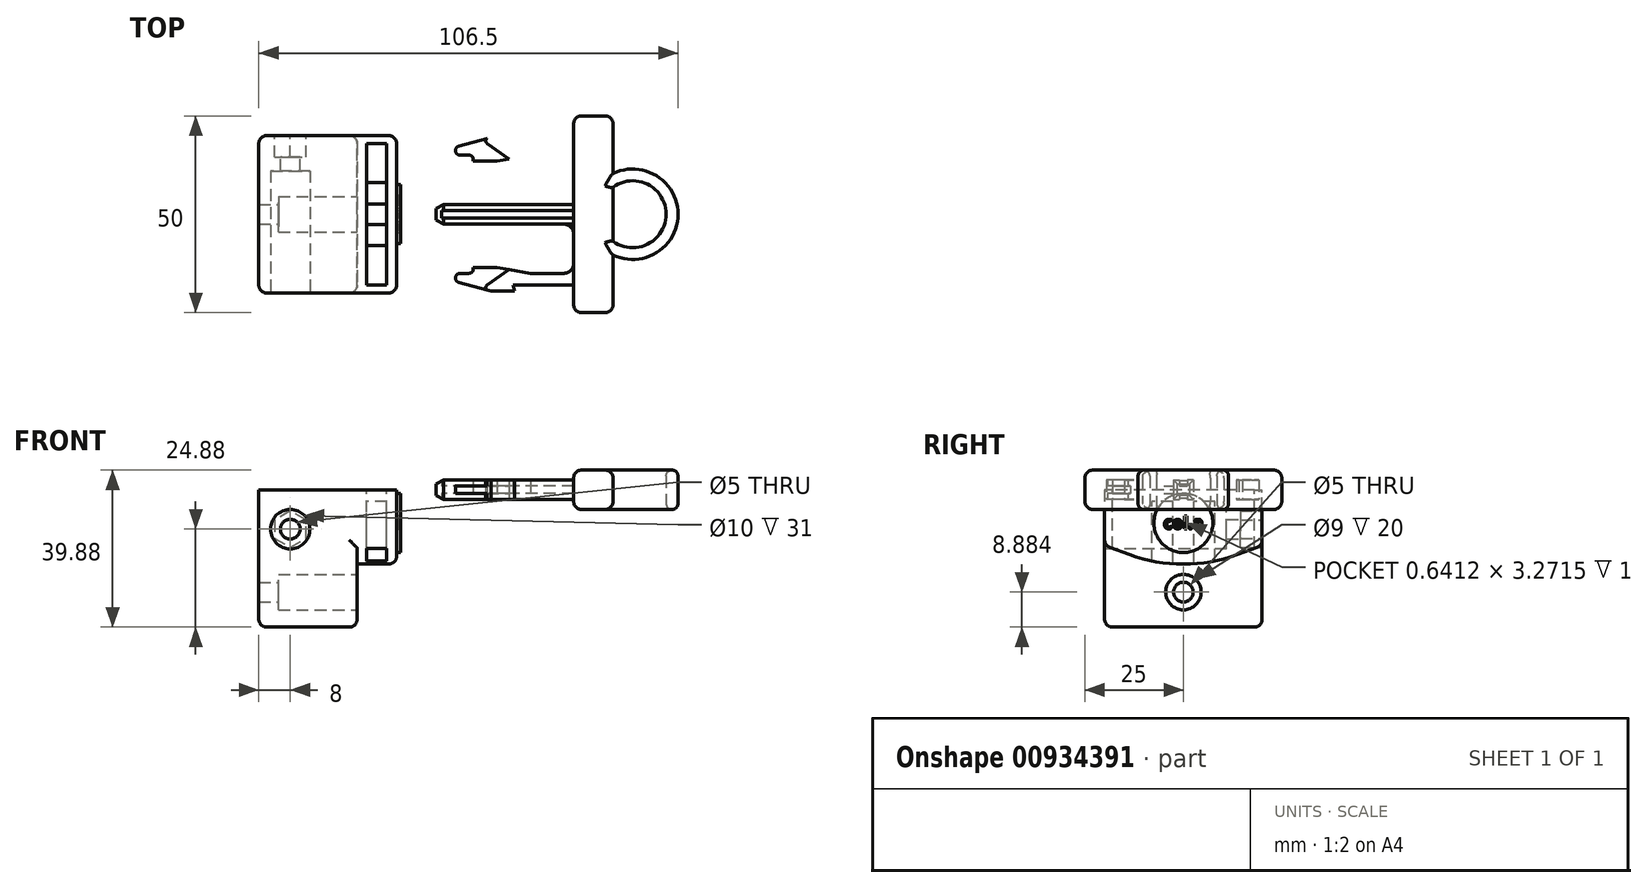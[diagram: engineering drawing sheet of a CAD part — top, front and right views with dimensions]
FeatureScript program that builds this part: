
annotation { "Feature Type Name" : "Feature", "Feature Type Description" : "" }
export const myFeature = defineFeature(function(context is Context, id is Id, definition is map)
    precondition{}
    {
        {
            var Q0;
            Q0=qCreatedBy(makeId("Top.planeOp"),FACE);
            var sketch = newSketch(context, id + "F0", { "sketchPlane" : qUnion([Q0])});
            skLineSegment(sketch, "E0.bottom", {"start": v(5, -25) * mm, "end": v(-5, -25) * mm});
            skLineSegment(sketch, "E0.top", {"start": v(5, 25) * mm, "end": v(-5, 25) * mm});
            skLineSegment(sketch, "E0.left", {"start": v(5, -25) * mm, "end": v(5, 25) * mm});
            skLineSegment(sketch, "E0.right", {"start": v(-5, -12.5) * mm, "end": v(-5, 12.5) * mm});
            skPoint(sketch, "E0.middle", {"position": v(0, 0) * mm});
            skLineSegment(sketch, "E1", {"start": v(-5, -18) * mm, "end": v(-20.4, -18) * mm});
            skLineSegment(sketch, "E2", {"start": v(-20.4, -18) * mm, "end": v(-20, -19.5) * mm});
            skLineSegment(sketch, "E3", {"start": v(-20, -19.5) * mm, "end": v(-26, -19.5) * mm});
            skLineSegment(sketch, "E4", {"start": v(-5, 0) * mm, "end": v(5, 0) * mm, "construction": true});
            skLineSegment(sketch, "E5.bottom", {"start": v(-5, 2.5) * mm, "end": v(-40, 2.5) * mm});
            skLineSegment(sketch, "E5.top", {"start": v(-5, -2.5) * mm, "end": v(-40, -2.5) * mm});
            skLineSegment(sketch, "E5.left", {"start": v(-5, 2.5) * mm, "end": v(-5, -2.5) * mm});
            skLineSegment(sketch, "E5.right", {"start": v(-40, 2.5) * mm, "end": v(-40, -2.5) * mm});
            skLineSegment(sketch, "E6", {"start": v(-7.5, -15) * mm, "end": v(-16, -15) * mm});
            skLineSegment(sketch, "E7", {"start": v(-16, -15) * mm, "end": v(-24.5, -13.5) * mm});
            skLineSegment(sketch, "E8", {"start": v(-24.5, -13.5) * mm, "end": v(-30.5, -13.5) * mm});
            skLineSegment(sketch, "E9", {"start": v(-30.5, -13.5) * mm, "end": v(-30.5, -14) * mm});
            skLineSegment(sketch, "E10", {"start": v(-31.5, -15) * mm, "end": v(-33.83, -15) * mm});
            skLineSegment(sketch, "E11", {"start": v(-34.14, -17.32) * mm, "end": v(-26, -19.5) * mm});
            skPoint(sketch, "E12.newPointA", {"position": v(-36.5, -15) * mm});
            skArc(sketch, "E12.filletArc", {"start": v(-33.83, -15) * mm, "mid": v(-35, -16.03) * mm, "end": v(-34.14, -17.32) * mm});
            skPoint(sketch, "E13.visualSharp", {"position": v(-30.5, -15) * mm});
            skArc(sketch, "E13.filletArc", {"start": v(-31.5, -15) * mm, "mid": v(-30.8, -14.7) * mm, "end": v(-30.5, -14) * mm});
            skLineSegment(sketch, "E14", {"start": v(-21.37, -14.05) * mm, "end": v(-27.01, -18) * mm});
            skArc(sketch, "E15", {"start": v(-27.01, -18) * mm, "mid": v(-27.33, -18.61) * mm, "end": v(-27.01, -19.23) * mm});
            skArc(sketch, "E16.MirrorCS", {"start": v(-31.5, 15) * mm, "mid": v(-30.8, 14.7) * mm, "end": v(-30.5, 14) * mm});
            skLineSegment(sketch, "E17.MirrorCS", {"start": v(-30.5, 13.5) * mm, "end": v(-30.5, 14) * mm});
            skArc(sketch, "E18.MirrorCS", {"start": v(-27.01, 18) * mm, "mid": v(-27.33, 18.61) * mm, "end": v(-27.01, 19.23) * mm});
            skLineSegment(sketch, "E19.MirrorCS", {"start": v(-20.4, 18) * mm, "end": v(-20, 19.5) * mm});
            skLineSegment(sketch, "E20.MirrorCS", {"start": v(-31.5, 15) * mm, "end": v(-33.83, 15) * mm});
            skLineSegment(sketch, "E21.MirrorCS", {"start": v(-20, 19.5) * mm, "end": v(-26, 19.5) * mm});
            skArc(sketch, "E22.MirrorCS", {"start": v(-33.83, 15) * mm, "mid": v(-35, 16.03) * mm, "end": v(-34.14, 17.32) * mm});
            skLineSegment(sketch, "E23.MirrorCS", {"start": v(-24.5, 13.5) * mm, "end": v(-30.5, 13.5) * mm});
            skPoint(sketch, "E24.MirrorP", {"position": v(-36.5, 15) * mm});
            skLineSegment(sketch, "E25.MirrorCS", {"start": v(-16, 15) * mm, "end": v(-24.5, 13.5) * mm});
            skLineSegment(sketch, "E26.MirrorCS", {"start": v(-5, 18) * mm, "end": v(-20.4, 18) * mm});
            skPoint(sketch, "E27.MirrorP", {"position": v(-30.5, 15) * mm});
            skLineSegment(sketch, "E28.MirrorCS", {"start": v(-7.5, 15) * mm, "end": v(-16, 15) * mm});
            skLineSegment(sketch, "E29.MirrorCS", {"start": v(-34.14, 17.32) * mm, "end": v(-26, 19.5) * mm});
            skLineSegment(sketch, "E30.MirrorCS", {"start": v(-21.37, 14.05) * mm, "end": v(-27.01, 18) * mm});
            skArc(sketch, "E31", {"start": v(-5, -5) * mm, "mid": v(-5.73, -3.23) * mm, "end": v(-7.5, -2.5) * mm});
            skArc(sketch, "E32.MirrorCS", {"start": v(-5, 5) * mm, "mid": v(-5.73, 3.23) * mm, "end": v(-7.5, 2.5) * mm});
            skPoint(sketch, "E33.newPointB", {"position": v(-5, -20) * mm});
            skArc(sketch, "E33.filletArc", {"start": v(-7.5, -15) * mm, "mid": v(-5.73, -14.27) * mm, "end": v(-5, -12.5) * mm});
            skPoint(sketch, "E34.newPointB", {"position": v(-5, 20) * mm});
            skArc(sketch, "E34.filletArc", {"start": v(-5, 12.5) * mm, "mid": v(-5.73, 14.27) * mm, "end": v(-7.5, 15) * mm});
            skLineSegment(sketch, "E35", {"start": v(-5, 18) * mm, "end": v(-5, 12.5) * mm});
            skLineSegment(sketch, "E36", {"start": v(-5, -12.5) * mm, "end": v(-5, -18) * mm});
            skLineSegment(sketch, "E37", {"start": v(-5, 25) * mm, "end": v(-5, 18) * mm});
            skLineSegment(sketch, "E38", {"start": v(-5, -25) * mm, "end": v(-5, -18) * mm});
            skLineSegment(sketch, "E39", {"start": v(-35.01, -19.06) * mm, "end": v(-35.01, -34.69) * mm, "construction": true});
            skLineSegment(sketch, "E40.0", {"start": v(-5, -1) * mm, "end": v(-38.5, -1) * mm});
            skLineSegment(sketch, "E40.2", {"start": v(-5, 1) * mm, "end": v(-38.5, 1) * mm});
            skLineSegment(sketch, "E40.3", {"start": v(-38.5, 1) * mm, "end": v(-38.5, -1) * mm});
            skSolve(sketch);
        }
        {
            var Q0;
            Q0=makeQuery(id+"F0.imprint","IMPRINT",FACE,{"disambiguationData":[TD([[makeQuery(id+"F0.imprint","IMPRINT",EDGE,{"derivedFrom":sQuery(id+"F0.wireOp",EDGE,"E0.bottom")}),-1.0]])]});
            extrude(context, id + "F1", {"entities" : qUnion([Q0]), "endBound" : BoundingType.SYMMETRIC, "depth" : 10 * mm, "offsetDistance" : 25 * mm});
        }
        {
            var Q0;
            Q0=makeQuery(id+"F0.imprint","IMPRINT",FACE,{"disambiguationData":[TD([[makeQuery(id+"F0.imprint","IMPRINT",EDGE,{"derivedFrom":sQuery(id+"F0.wireOp",EDGE,"E16.MirrorCS")}),1.0]])]});
            var Q1;
            {var subQ5=sQuery(id+"F0.wireOp",EDGE,"E18.MirrorCS");Q1=makeQuery(id+"F0.imprint","IMPRINT",FACE,{"disambiguationData":[TD([[makeQuery(id+"F0.imprint","IMPRINT",EDGE,{"derivedFrom":subQ5}),-1.0]])]});}
            var Q2;
            {var subQ0=sQuery(id+"F0.wireOp",EDGE,"E8");Q2=makeQuery(id+"F0.imprint","IMPRINT",FACE,{"disambiguationData":[TD([[makeQuery(id+"F0.imprint","IMPRINT",EDGE,{"derivedFrom":subQ0}),1.0]])]});}
            var Q3;
            Q3=makeQuery(id+"F0.imprint","IMPRINT",FACE,{"disambiguationData":[TD([[makeQuery(id+"F0.imprint","IMPRINT",EDGE,{"derivedFrom":sQuery(id+"F0.wireOp",EDGE,"E1")}),-1.0]])]});
            var Q4;
            {var subQ3=sQuery(id+"F0.wireOp",EDGE,"E32.MirrorCS");Q4=makeQuery(id+"F0.imprint","IMPRINT",FACE,{"disambiguationData":[TD([[makeQuery(id+"F0.imprint","IMPRINT",EDGE,{"derivedFrom":subQ3}),1.0]])]});}
            var Q5;
            {var subQ3=sQuery(id+"F0.wireOp",EDGE,"E31");Q5=makeQuery(id+"F0.imprint","IMPRINT",FACE,{"disambiguationData":[TD([[makeQuery(id+"F0.imprint","IMPRINT",EDGE,{"derivedFrom":subQ3}),-1.0]])]});}
            var Q6;
            Q6=makeQuery(id+"F0.imprint","IMPRINT",FACE,{"disambiguationData":[TD([[makeQuery(id+"F0.imprint","IMPRINT",EDGE,{"derivedFrom":sQuery(id+"F0.wireOp",EDGE,"E40.0")}),-1.0]])]});
            extrude(context, id + "F2", {"entities" : qUnion([Q0, Q1, Q2, Q3, Q4, Q5, Q6]), "operationType" : NewBodyOperationType.ADD, "endBound" : BoundingType.SYMMETRIC, "depth" : 2 * mm, "offsetDistance" : 25 * mm});
        }
        {
            var Q0;
            {var subQ5=sQuery(id+"F0.wireOp",EDGE,"E18.MirrorCS");Q0=makeQuery(id+"F0.imprint","IMPRINT",FACE,{"disambiguationData":[TD([[makeQuery(id+"F0.imprint","IMPRINT",EDGE,{"derivedFrom":subQ5}),-1.0]])]});}
            var Q1;
            Q1=makeQuery(id+"F0.imprint","IMPRINT",FACE,{"disambiguationData":[TD([[makeQuery(id+"F0.imprint","IMPRINT",EDGE,{"derivedFrom":sQuery(id+"F0.wireOp",EDGE,"E1")}),-1.0]])]});
            var Q2;
            Q2=makeQuery(id+"F0.imprint","IMPRINT",FACE,{"disambiguationData":[TD([[makeQuery(id+"F0.imprint","IMPRINT",EDGE,{"derivedFrom":sQuery(id+"F0.wireOp",EDGE,"E5.bottom")}),1.0]])]});
            extrude(context, id + "F3", {"entities" : qUnion([Q0, Q1, Q2]), "operationType" : NewBodyOperationType.ADD, "endBound" : BoundingType.SYMMETRIC, "depth" : 5 * mm, "offsetDistance" : 25 * mm});
        }
        {
            var Q0;
            Q0=makeQuery(id+"F3.opExtrude","CAP_EDGE",EDGE,{"disambiguationData":[OSD([sQuery(id+"F0.wireOp",EDGE,"E5.right")])],"isStart":true});
            var Q1;
            Q1=makeQuery(id+"F3.opExtrude","SWEPT_EDGE",EDGE,{"disambiguationData":[OSD([sQuery(id+"F0.wireOp",EDGE,"E5.top"),sQuery(id+"F0.wireOp",EDGE,"E5.right")])]});
            var Q2;
            Q2=makeQuery(id+"F3.opExtrude","CAP_EDGE",EDGE,{"disambiguationData":[OSD([sQuery(id+"F0.wireOp",EDGE,"E5.right")])],"isStart":false});
            var Q3;
            Q3=makeQuery(id+"F3.opExtrude","SWEPT_EDGE",EDGE,{"disambiguationData":[OSD([sQuery(id+"F0.wireOp",EDGE,"E5.bottom"),sQuery(id+"F0.wireOp",EDGE,"E5.right")])]});
            chamfer(context, id + "F4", {"entities" : qUnion([Q0, Q1, Q2, Q3]), "chamferType" : ChamferType.TWO_OFFSETS, "width1" : 1 * mm, "oppositeDirection" : false, "width2" : 2 * mm, "tangentPropagation" : true});
        }
        {
            var Q0;
            Q0=makeQuery(id+"F1.opExtrude","CAP_EDGE",EDGE,{"disambiguationData":[OSD([sQuery(id+"F0.wireOp",EDGE,"E0.bottom")])],"isStart":true});
            var Q1;
            Q1=makeQuery(id+"F1.opExtrude","CAP_EDGE",EDGE,{"disambiguationData":[OSD([sQuery(id+"F0.wireOp",EDGE,"E0.right"),sQuery(id+"F0.wireOp",EDGE,"E5.left"),sQuery(id+"F0.wireOp",EDGE,"E35"),sQuery(id+"F0.wireOp",EDGE,"E36"),sQuery(id+"F0.wireOp",EDGE,"E37"),sQuery(id+"F0.wireOp",EDGE,"E38")])],"isStart":true});
            var Q2;
            Q2=makeQuery(id+"F1.opExtrude","CAP_EDGE",EDGE,{"disambiguationData":[OSD([sQuery(id+"F0.wireOp",EDGE,"E0.left")])],"isStart":true});
            var Q3;
            Q3=makeQuery(id+"F1.opExtrude","SWEPT_EDGE",EDGE,{"disambiguationData":[OSD([sQuery(id+"F0.wireOp",EDGE,"E0.bottom"),sQuery(id+"F0.wireOp",EDGE,"E38")])]});
            var Q4;
            Q4=makeQuery(id+"F1.opExtrude","SWEPT_EDGE",EDGE,{"disambiguationData":[OSD([sQuery(id+"F0.wireOp",EDGE,"E0.bottom"),sQuery(id+"F0.wireOp",EDGE,"E0.left")])]});
            var Q5;
            Q5=makeQuery(id+"F1.opExtrude","CAP_EDGE",EDGE,{"disambiguationData":[OSD([sQuery(id+"F0.wireOp",EDGE,"E0.bottom")])],"isStart":false});
            var Q6;
            Q6=makeQuery(id+"F1.opExtrude","CAP_EDGE",EDGE,{"disambiguationData":[OSD([sQuery(id+"F0.wireOp",EDGE,"E0.left")])],"isStart":false});
            var Q7;
            Q7=makeQuery(id+"F1.opExtrude","CAP_EDGE",EDGE,{"disambiguationData":[OSD([sQuery(id+"F0.wireOp",EDGE,"E0.top")])],"isStart":false});
            var Q8;
            Q8=makeQuery(id+"F1.opExtrude","CAP_EDGE",EDGE,{"disambiguationData":[OSD([sQuery(id+"F0.wireOp",EDGE,"E0.right"),sQuery(id+"F0.wireOp",EDGE,"E5.left"),sQuery(id+"F0.wireOp",EDGE,"E35"),sQuery(id+"F0.wireOp",EDGE,"E36"),sQuery(id+"F0.wireOp",EDGE,"E37"),sQuery(id+"F0.wireOp",EDGE,"E38")])],"isStart":false});
            var Q9;
            Q9=makeQuery(id+"F1.opExtrude","SWEPT_EDGE",EDGE,{"disambiguationData":[OSD([sQuery(id+"F0.wireOp",EDGE,"E0.top"),sQuery(id+"F0.wireOp",EDGE,"E37")])]});
            var Q10;
            Q10=makeQuery(id+"F1.opExtrude","SWEPT_EDGE",EDGE,{"disambiguationData":[OSD([sQuery(id+"F0.wireOp",EDGE,"E0.top"),sQuery(id+"F0.wireOp",EDGE,"E0.left")])]});
            var Q11;
            Q11=makeQuery(id+"F1.opExtrude","CAP_EDGE",EDGE,{"disambiguationData":[OSD([sQuery(id+"F0.wireOp",EDGE,"E0.top")])],"isStart":true});
            fillet(context, id + "F5", {"entities" : qUnion([Q0, Q1, Q2, Q3, Q4, Q5, Q6, Q7, Q8, Q9, Q10, Q11]), "radius" : 2 * mm, "tangentPropagation" : true, "allowEdgeOverflow" : false});
        }
        {
            var Q0;
            Q0=qCreatedBy(makeId("Front.planeOp"),FACE);
            var sketch = newSketch(context, id + "F6", { "sketchPlane" : qUnion([Q0])});
            skLineSegment(sketch, "E41.bottom", {"start": v(0, -5) * mm, "end": v(0, -5) * mm});
            skLineSegment(sketch, "E41.top", {"start": v(0, 5) * mm, "end": v(0, 5) * mm});
            skLineSegment(sketch, "E41.left", {"start": v(1.5, -3.5) * mm, "end": v(1.5, 3.5) * mm});
            skLineSegment(sketch, "E41.right", {"start": v(-1.5, -3.5) * mm, "end": v(-1.5, 3.5) * mm});
            skPoint(sketch, "E41.middle", {"position": v(0, 0) * mm});
            skPoint(sketch, "E42.visualSharp", {"position": v(-1.5, 5) * mm});
            skArc(sketch, "E42.filletArc", {"start": v(0, 5) * mm, "mid": v(-1.06, 4.56) * mm, "end": v(-1.5, 3.5) * mm});
            skPoint(sketch, "E43.visualSharp", {"position": v(1.5, 5) * mm});
            skArc(sketch, "E43.filletArc", {"start": v(1.5, 3.5) * mm, "mid": v(1.06, 4.56) * mm, "end": v(0, 5) * mm});
            skPoint(sketch, "E44.visualSharp", {"position": v(1.5, -5) * mm});
            skArc(sketch, "E44.filletArc", {"start": v(0, -5) * mm, "mid": v(1.06, -4.56) * mm, "end": v(1.5, -3.5) * mm});
            skPoint(sketch, "E45.visualSharp", {"position": v(-1.5, -5) * mm});
            skArc(sketch, "E45.filletArc", {"start": v(-1.5, -3.5) * mm, "mid": v(-1.06, -4.56) * mm, "end": v(0, -5) * mm});
            skLineSegment(sketch, "E46", {"start": v(0, 0) * mm, "end": v(10, 0) * mm, "construction": true});
            skLineSegment(sketch, "E47", {"start": v(10, 0) * mm, "end": v(10, 4.4) * mm, "construction": true});
            skSolve(sketch);
        }
        {
            var Q0;
            Q0 = qSketchRegion(id + "F6", true);
            var Q1;
            Q1=sQuery(id+"F6.wireOp",EDGE,"E47");
            revolve(context, id + "F7", {"operationType" : NewBodyOperationType.ADD, "surfaceOperationType" : NewSurfaceOperationType.NEW, "entities" : qUnion([Q0]), "axis" : qUnion([Q1]), "revolveType" : RevolveType.FULL});
        }
        {
            var Q0;
            Q0=qCreatedBy(makeId("Top.planeOp"),FACE);
            var sketch = newSketch(context, id + "F8", { "sketchPlane" : qUnion([Q0])});
            skLineSegment(sketch, "E48.bottom", {"start": v(-52.5, -2.65) * mm, "end": v(-57.6, -2.65) * mm});
            skLineSegment(sketch, "E48.top", {"start": v(-52.5, 2.65) * mm, "end": v(-57.6, 2.65) * mm});
            skLineSegment(sketch, "E48.left", {"start": v(-52.5, -2.65) * mm, "end": v(-52.5, 2.65) * mm});
            skLineSegment(sketch, "E48.right", {"start": v(-57.6, -2.65) * mm, "end": v(-57.6, 2.65) * mm});
            skPoint(sketch, "E48.middle", {"position": v(-55.05, 0) * mm});
            skLineSegment(sketch, "E49.bottom", {"start": v(-52.5, 18) * mm, "end": v(-57.6, 18) * mm});
            skLineSegment(sketch, "E49.top", {"start": v(-52.5, 8) * mm, "end": v(-57.6, 8) * mm});
            skLineSegment(sketch, "E49.left", {"start": v(-52.5, 18) * mm, "end": v(-52.5, 8) * mm});
            skLineSegment(sketch, "E49.right", {"start": v(-57.6, 18) * mm, "end": v(-57.6, 8) * mm});
            skPoint(sketch, "E49.middle", {"position": v(-55.05, 13) * mm});
            skPoint(sketch, "E49.middle.positionSnap0", {"position": v(-55.05, 2.65) * mm});
            skPoint(sketch, "E49.centerSnap0", {"position": v(-55.05, 2.65) * mm});
            skLineSegment(sketch, "E50.bottom", {"start": v(-52.5, -18) * mm, "end": v(-57.6, -18) * mm});
            skLineSegment(sketch, "E50.top", {"start": v(-52.5, -8) * mm, "end": v(-57.6, -8) * mm});
            skLineSegment(sketch, "E50.left", {"start": v(-52.5, -18) * mm, "end": v(-52.5, -8) * mm});
            skLineSegment(sketch, "E50.right", {"start": v(-57.6, -18) * mm, "end": v(-57.6, -8) * mm});
            skPoint(sketch, "E50.middle", {"position": v(-55.05, -13) * mm});
            skLineSegment(sketch, "E51.bottom", {"start": v(-57.6, 18) * mm, "end": v(-52.5, 18) * mm});
            skLineSegment(sketch, "E51.top", {"start": v(-57.6, -18) * mm, "end": v(-52.5, -18) * mm});
            skLineSegment(sketch, "E51.left", {"start": v(-57.6, 18) * mm, "end": v(-57.6, -18) * mm});
            skLineSegment(sketch, "E51.right", {"start": v(-52.5, 18) * mm, "end": v(-52.5, -18) * mm});
            skLineSegment(sketch, "E52", {"start": v(-50, 28.03) * mm, "end": v(-50, -31.97) * mm, "construction": true});
            skLineSegment(sketch, "E53", {"start": v(0, 0) * mm, "end": v(-100, 0) * mm, "construction": true});
            skSolve(sketch);
        }
        {
            var Q0;
            Q0=sQuery(id+"F8.wireOp",EDGE,"E52");
            cPlane(context, id + "F9", {"entities" : qUnion([Q0]), "cplaneType" : CPlaneType.LINE_ANGLE, "offset" : 25 * mm, "angle" : 90 * degree, "width" : 150 * mm, "height" : 150 * mm});
        }
        {
            var Q0;
            Q0=qCreatedBy(id+"F9.planeOp",FACE);
            var sketch = newSketch(context, id + "F10", { "sketchPlane" : qUnion([Q0])});
            skLineSegment(sketch, "E54", {"start": v(20, 0) * mm, "end": v(-20, 0) * mm});
            skLineSegment(sketch, "E55", {"start": v(-20, 0) * mm, "end": v(-20, -14.17) * mm});
            skLineSegment(sketch, "E56", {"start": v(-20, -14.17) * mm, "end": v(-13.68, -16.47) * mm});
            skLineSegment(sketch, "E57", {"start": v(13.68, -16.47) * mm, "end": v(20, -14.17) * mm});
            skLineSegment(sketch, "E58", {"start": v(20, -14.17) * mm, "end": v(20, 0) * mm});
            skPoint(sketch, "E59.visualSharp", {"position": v(0, -21.45) * mm});
            skArc(sketch, "E59.filletArc", {"start": v(-13.68, -16.47) * mm, "mid": v(0, -18.88) * mm, "end": v(13.68, -16.47) * mm});
            skLineSegment(sketch, "E60", {"start": v(-18, 0) * mm, "end": v(-18, -14.9) * mm, "construction": true});
            skSolve(sketch);
        }
        {
            var Q0;
            Q0 = qSketchRegion(id + "F10", true);
            extrude(context, id + "F11", {"entities" : qUnion([Q0]), "oppositeDirection" : true, "depth" : 10 * mm, "offsetDistance" : 25 * mm});
        }
        {
            var Q0;
            {var subQ0=sQuery(id+"F8.wireOp",EDGE,"E49.top");Q0=makeQuery(id+"F8.imprint","IMPRINT",FACE,{"disambiguationData":[TD([[makeQuery(id+"F8.imprint","IMPRINT",EDGE,{"derivedFrom":subQ0}),-1.0]])]});}
            var Q1;
            {var subQ0=sQuery(id+"F8.wireOp",EDGE,"E48.bottom");Q1=makeQuery(id+"F8.imprint","IMPRINT",FACE,{"disambiguationData":[TD([[makeQuery(id+"F8.imprint","IMPRINT",EDGE,{"derivedFrom":subQ0}),-1.0]])]});}
            var Q2;
            {var subQ0=sQuery(id+"F8.wireOp",EDGE,"E50.top");Q2=makeQuery(id+"F8.imprint","IMPRINT",FACE,{"disambiguationData":[TD([[makeQuery(id+"F8.imprint","IMPRINT",EDGE,{"derivedFrom":subQ0}),1.0]])]});}
            extrude(context, id + "F12", {"entities" : qUnion([Q0, Q1, Q2]), "operationType" : NewBodyOperationType.REMOVE, "endBound" : BoundingType.THROUGH_ALL, "oppositeDirection" : true, "depth" : 25 * mm, "offsetDistance" : 25 * mm});
        }
        {
            var Q0;
            Q0=makeQuery(id+"F11.opExtrude","CAP_FACE",FACE,{"disambiguationData":[OSD([sQuery(id+"F10.wireOp",EDGE,"E54"),sQuery(id+"F10.wireOp",EDGE,"E55"),sQuery(id+"F10.wireOp",EDGE,"E56"),sQuery(id+"F10.wireOp",EDGE,"E57"),sQuery(id+"F10.wireOp",EDGE,"E58"),sQuery(id+"F10.wireOp",EDGE,"E59.filletArc")])],"isStart":false});
            var sketch = newSketch(context, id + "F13", { "sketchPlane" : qUnion([Q0])});
            skLineSegment(sketch, "E61.bottom", {"start": v(-20, 0) * mm, "end": v(20, 0) * mm});
            skLineSegment(sketch, "E61.top", {"start": v(-20, -34.88) * mm, "end": v(20, -34.88) * mm});
            skLineSegment(sketch, "E61.left", {"start": v(-20, 0) * mm, "end": v(-20, -34.88) * mm});
            skLineSegment(sketch, "E61.right", {"start": v(20, 0) * mm, "end": v(20, -34.88) * mm});
            skSolve(sketch);
        }
        {
            var Q0;
            Q0 = qSketchRegion(id + "F13", true);
            extrude(context, id + "F14", {"entities" : qUnion([Q0]), "operationType" : NewBodyOperationType.ADD, "depth" : 25 * mm, "offsetDistance" : 25 * mm});
        }
        {
            var Q0;
            {var subQ0=sQuery(id+"F8.wireOp",EDGE,"E48.top");Q0=makeQuery(id+"F8.imprint","IMPRINT",FACE,{"disambiguationData":[TD([[makeQuery(id+"F8.imprint","IMPRINT",EDGE,{"derivedFrom":subQ0}),-1.0]])]});}
            var Q1;
            {var subQ0=sQuery(id+"F8.wireOp",EDGE,"E48.bottom");Q1=makeQuery(id+"F8.imprint","IMPRINT",FACE,{"disambiguationData":[TD([[makeQuery(id+"F8.imprint","IMPRINT",EDGE,{"derivedFrom":subQ0}),1.0]])]});}
            extrude(context, id + "F15", {"entities" : qUnion([Q0, Q1]), "operationType" : NewBodyOperationType.REMOVE, "oppositeDirection" : true, "depth" : 3 * mm, "offsetDistance" : 25 * mm});
        }
        {
            var Q0;
            Q0=makeQuery(id+"F11.opExtrude","SWEPT_EDGE",EDGE,{"disambiguationData":[OSD([sQuery(id+"F10.wireOp",EDGE,"E57"),sQuery(id+"F10.wireOp",EDGE,"E58")])]});
            var Q1;
            Q1=makeQuery(id+"F11.opExtrude","SWEPT_EDGE",EDGE,{"disambiguationData":[OSD([sQuery(id+"F10.wireOp",EDGE,"E55"),sQuery(id+"F10.wireOp",EDGE,"E56")])]});
            var Q2;
            Q2=makeQuery(id+"F11.opExtrude","CAP_EDGE",EDGE,{"disambiguationData":[OSD([sQuery(id+"F10.wireOp",EDGE,"E59.filletArc")])],"isStart":true});
            var Q3;
            Q3=makeQuery(id+"F14.opExtrude","CAP_EDGE",EDGE,{"disambiguationData":[OSD([sQuery(id+"F13.wireOp",EDGE,"E61.left")])],"isStart":true});
            var Q4;
            Q4=makeQuery(id+"F14.opExtrude","CAP_EDGE",EDGE,{"disambiguationData":[OSD([sQuery(id+"F13.wireOp",EDGE,"E61.right")])],"isStart":true});
            var Q5;
            Q5=makeQuery(id+"F14.opExtrude","CAP_EDGE",EDGE,{"disambiguationData":[OSD([sQuery(id+"F13.wireOp",EDGE,"E61.top")])],"isStart":true});
            var Q6;
            Q6=makeQuery(id+"F14.opExtrude","SWEPT_EDGE",EDGE,{"disambiguationData":[OSD([sQuery(id+"F13.wireOp",EDGE,"E61.top"),sQuery(id+"F13.wireOp",EDGE,"E61.left")])]});
            var Q7;
            Q7=makeQuery(id+"F14.opExtrude","SWEPT_EDGE",EDGE,{"disambiguationData":[OSD([sQuery(id+"F13.wireOp",EDGE,"E61.top"),sQuery(id+"F13.wireOp",EDGE,"E61.right")])]});
            var Q8;
            Q8=makeQuery(id+"F14.opExtrude","CAP_EDGE",EDGE,{"disambiguationData":[OSD([sQuery(id+"F13.wireOp",EDGE,"E61.top")])],"isStart":false});
            var Q9;
            Q9=makeQuery(id+"F14.opExtrude","CAP_EDGE",EDGE,{"disambiguationData":[OSD([sQuery(id+"F13.wireOp",EDGE,"E61.left")])],"isStart":false});
            var Q10;
            Q10=makeQuery(id+"F11.opExtrude","CAP_EDGE",EDGE,{"disambiguationData":[OSD([sQuery(id+"F10.wireOp",EDGE,"E58")])],"isStart":true});
            var Q11;
            Q11=makeQuery(id+"F11.opExtrude","CAP_EDGE",EDGE,{"disambiguationData":[OSD([sQuery(id+"F10.wireOp",EDGE,"E55")])],"isStart":true});
            var Q12;
            Q12=makeQuery(id+"F14.opExtrude","CAP_EDGE",EDGE,{"disambiguationData":[OSD([sQuery(id+"F13.wireOp",EDGE,"E61.right")])],"isStart":false});
            fillet(context, id + "F16", {"entities" : qUnion([Q0, Q1, Q2, Q3, Q4, Q5, Q6, Q7, Q8, Q9, Q10, Q11, Q12]), "radius" : 2 * mm, "tangentPropagation" : true, "allowEdgeOverflow" : false});
        }
        {
            var Q0;
            Q0=makeQuery(id+"F14.opExtrude","CAP_FACE",FACE,{"disambiguationData":[OSD([sQuery(id+"F13.wireOp",EDGE,"E61.bottom"),sQuery(id+"F13.wireOp",EDGE,"E61.top"),sQuery(id+"F13.wireOp",EDGE,"E61.left"),sQuery(id+"F13.wireOp",EDGE,"E61.right")])],"isStart":true});
            var sketch = newSketch(context, id + "F17", { "sketchPlane" : qUnion([Q0])});
            skLineSegment(sketch, "E62", {"start": v(-18, -26) * mm, "end": v(18, -26) * mm, "construction": true});
            skLineSegment(sketch, "E63", {"start": v(0, -32.88) * mm, "end": v(0, -18.88) * mm, "construction": true});
            skPoint(sketch, "E64", {"position": v(0, -26) * mm});
            skSolve(sketch);
        }
        {
            var Q0;
            Q0=sQuery(id+"F17.wireOp",VERTEX,"E64");
            var Q1;
            Q1=makeQuery(id+"F11.opExtrude","SWEPT_BODY",BODY,{"disambiguationData":[OSD([sQuery(id+"F10.wireOp",EDGE,"E54"),sQuery(id+"F10.wireOp",EDGE,"E55"),sQuery(id+"F10.wireOp",EDGE,"E56"),sQuery(id+"F10.wireOp",EDGE,"E57"),sQuery(id+"F10.wireOp",EDGE,"E58"),sQuery(id+"F10.wireOp",EDGE,"E59.filletArc")])]});
            hole(context, id + "F18", {"style" : HoleStyle.C_BORE, "endStyle" : HoleEndStyle.THROUGH, "holeDiameter" : 5 * mm, "cBoreDiameter" : 9 * mm, "cBoreDepth" : 20 * mm, "majorDiameter" : 5 * mm, "isTappedThrough" : true, "tappedDepth" : 12 * mm, "tapClearance" : 3, "locations" : qUnion([Q0]), "scope" : qUnion([Q1])});
        }
        {
            var Q0;
            Q0=makeQuery(id+"F11.opExtrude","CAP_FACE",FACE,{"disambiguationData":[OSD([sQuery(id+"F10.wireOp",EDGE,"E54"),sQuery(id+"F10.wireOp",EDGE,"E55"),sQuery(id+"F10.wireOp",EDGE,"E56"),sQuery(id+"F10.wireOp",EDGE,"E57"),sQuery(id+"F10.wireOp",EDGE,"E58"),sQuery(id+"F10.wireOp",EDGE,"E59.filletArc")])],"isStart":true});
            var sketch = newSketch(context, id + "F19", { "sketchPlane" : qUnion([Q0])});
            skLineSegment(sketch, "E65", {"start": v(0, -16.88) * mm, "end": v(0, 0) * mm, "construction": true});
            skCircle(sketch, "E66", {"center": v(0, -8.44) * mm, "radius": 7.5 * mm});
            skText(sketch, "E67", { "text": "col.a", "fontName": "OpenSans-Bold.ttf"});
            const initialGuessF19  = {"E67": [-0.005, -0.0099, 1, 0, 0.0031]};
            skSetInitialGuess(sketch, initialGuessF19);
            skSolve(sketch);
        }
        {
            var Q0;
            Q0=makeQuery(id+"F19.imprint","IMPRINT",FACE,{"disambiguationData":[TD([[makeQuery(id+"F19.imprint","IMPRINT",EDGE,{"derivedFrom":sQuery(id+"F19.wireOp",EDGE,"E66")}),1.0]])]});
            var Q1;
            Q1=makeQuery(id+"F19.imprint","IMPRINT",FACE,{"disambiguationData":[TD([[makeQuery(id+"F19.imprint","IMPRINT",EDGE,{"derivedFrom":sQuery(id+"F19.wireOp",EDGE,"E67.sketch_text.stroke-14")}),1.0]])]});
            var Q2;
            Q2=makeQuery(id+"F19.imprint","IMPRINT",FACE,{"disambiguationData":[TD([[makeQuery(id+"F19.imprint","IMPRINT",EDGE,{"derivedFrom":sQuery(id+"F19.wireOp",EDGE,"E67.sketch_text.stroke-62")}),1.0]])]});
            extrude(context, id + "F20", {"entities" : qUnion([Q0, Q1, Q2]), "operationType" : NewBodyOperationType.ADD, "depth" : 1 * mm, "offsetDistance" : 25 * mm});
        }
        {
            var Q0;
            Q0=makeQuery(id+"F14.boolean.opBoolean","MERGE",FACE,{"derivedFrom":[makeQuery(id+"F11.opExtrude","SWEPT_FACE",FACE,{"disambiguationData":[OSD([sQuery(id+"F10.wireOp",EDGE,"E58")])]}),makeQuery(id+"F14.opExtrude","SWEPT_FACE",FACE,{"disambiguationData":[OSD([sQuery(id+"F13.wireOp",EDGE,"E61.left")])]})]});
            var sketch = newSketch(context, id + "F21", { "sketchPlane" : qUnion([Q0])});
            skCircle(sketch, "E68.cCircle", {"center": v(77, -10) * mm, "radius": 4 * mm, "construction": true});
            skLineSegment(sketch, "E68.0", {"start": v(73, -12.3) * mm, "end": v(73, -7.7) * mm});
            skLineSegment(sketch, "E68.1", {"start": v(73, -7.7) * mm, "end": v(77, -5.38) * mm});
            skLineSegment(sketch, "E68.2", {"start": v(77, -5.38) * mm, "end": v(81, -7.7) * mm});
            skLineSegment(sketch, "E68.3", {"start": v(81, -7.7) * mm, "end": v(81, -12.3) * mm});
            skLineSegment(sketch, "E68.4", {"start": v(81, -12.3) * mm, "end": v(77, -14.62) * mm});
            skLineSegment(sketch, "E68.5", {"start": v(77, -14.62) * mm, "end": v(73, -12.3) * mm});
            skPoint(sketch, "E68.0.midPoint", {"position": v(73, -10) * mm});
            skCircle(sketch, "E69", {"center": v(77, -10) * mm, "radius": 2.5 * mm});
            skSolve(sketch);
        }
        {
            var Q0;
            Q0 = qSketchRegion(id + "F21", true);
            extrude(context, id + "F22", {"entities" : qUnion([Q0]), "operationType" : NewBodyOperationType.REMOVE, "oppositeDirection" : true, "depth" : 5.5 * mm, "offsetDistance" : 25 * mm});
        }
        {
            var Q0;
            Q0=makeQuery(id+"F22.boolean.opBoolean","SPLIT",FACE,{"disambiguationData":[TD([makeQuery(id+"F22.opExtrude","SWEPT_FACE",FACE,{"disambiguationData":[OSD([sQuery(id+"F21.wireOp",EDGE,"E69")])]})])],"derivedFrom":makeQuery(id+"F14.boolean.opBoolean","MERGE",FACE,{"derivedFrom":[makeQuery(id+"F11.opExtrude","SWEPT_FACE",FACE,{"disambiguationData":[OSD([sQuery(id+"F10.wireOp",EDGE,"E58")])]}),makeQuery(id+"F14.opExtrude","SWEPT_FACE",FACE,{"disambiguationData":[OSD([sQuery(id+"F13.wireOp",EDGE,"E61.left")])]})]})});
            extrude(context, id + "F23", {"entities" : qUnion([Q0]), "operationType" : NewBodyOperationType.REMOVE, "endBound" : BoundingType.THROUGH_ALL, "oppositeDirection" : true, "depth" : 25 * mm, "offsetDistance" : 25 * mm});
        }
        {
            var Q0;
            Q0=makeQuery(id+"F14.boolean.opBoolean","MERGE",FACE,{"derivedFrom":[makeQuery(id+"F11.opExtrude","SWEPT_FACE",FACE,{"disambiguationData":[OSD([sQuery(id+"F10.wireOp",EDGE,"E55")])]}),makeQuery(id+"F14.opExtrude","SWEPT_FACE",FACE,{"disambiguationData":[OSD([sQuery(id+"F13.wireOp",EDGE,"E61.right")])]})]});
            var sketch = newSketch(context, id + "F24", { "sketchPlane" : qUnion([Q0])});
            skCircle(sketch, "E70", {"center": v(-77, -10) * mm, "radius": 5 * mm});
            skSolve(sketch);
        }
        {
            var Q0;
            Q0=makeQuery(id+"F24.imprint","IMPRINT",FACE,{"disambiguationData":[TD([[makeQuery(id+"F24.imprint","IMPRINT",EDGE,{"derivedFrom":sQuery(id+"F24.wireOp",EDGE,"E70")}),1.0]])]});
            extrude(context, id + "F25", {"entities" : qUnion([Q0]), "operationType" : NewBodyOperationType.REMOVE, "oppositeDirection" : true, "depth" : 31 * mm, "offsetDistance" : 25 * mm});
        }
    });
